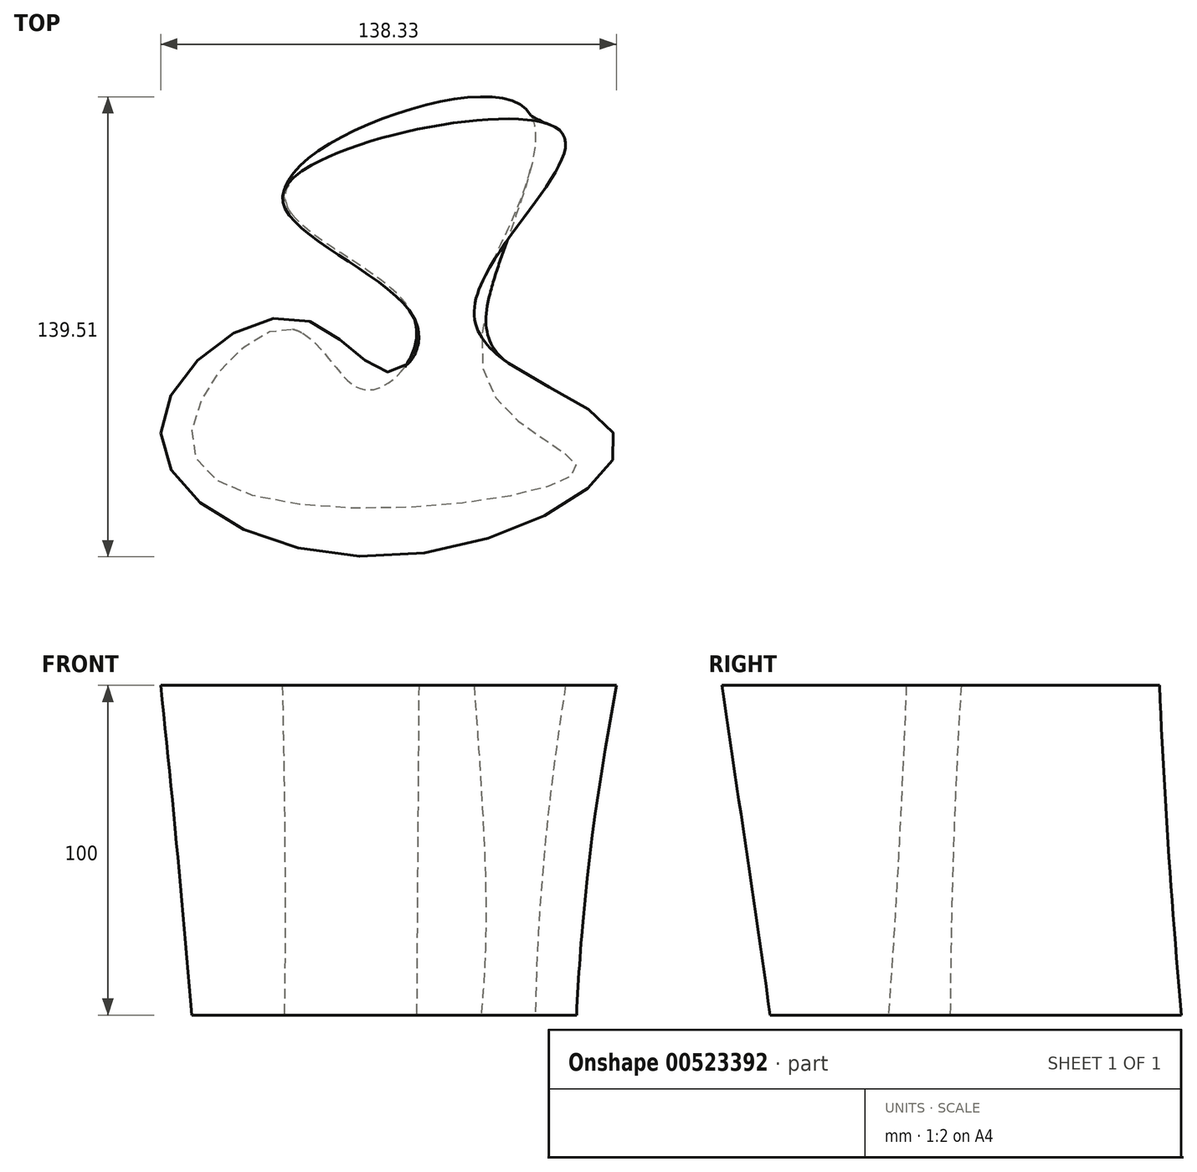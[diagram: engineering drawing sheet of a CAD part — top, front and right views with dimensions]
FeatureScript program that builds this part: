
annotation { "Feature Type Name" : "Feature", "Feature Type Description" : "" }
export const myFeature = defineFeature(function(context is Context, id is Id, definition is map)
    precondition{}
    {
        {
            var Q0;
            Q0=qCreatedBy(makeId("Top.planeOp"),FACE);
            cPlane(context, id + "F0", {"entities" : qUnion([Q0]), "cplaneType" : CPlaneType.OFFSET, "offset" : 100 * mm, "width" : 150 * mm, "height" : 150 * mm});
        }
        {
            var Q0;
            Q0=qCreatedBy(makeId("Top.planeOp"),FACE);
            var sketch = newSketch(context, id + "F1", { "sketchPlane" : qUnion([Q0])});
            skFitSpline(sketch, "E0", {"points": [v(0, 0) * mm, v(-39.28, 38.78) * mm, v(33.62, 63.74) * mm, v(21.63, -18.14) * mm, v(48.93, -46.76) * mm, v(-64.9, -44.77) * mm, v(-38.94, -3.16) * mm, v(-14.98, -21.8) * mm, v(0, 0) * mm]});
            skSolve(sketch);
        }
        {
            var Q0;
            Q0=qCreatedBy(id+"F0.planeOp",FACE);
            var sketch = newSketch(context, id + "F2", { "sketchPlane" : qUnion([Q0])});
            skFitSpline(sketch, "E1", {"points": [v(0, 0) * mm, v(-39.6, 38.44) * mm, v(44.93, 56.08) * mm, v(18.3, 0) * mm, v(60.91, -35.78) * mm, v(-8.99, -72.4) * mm, v(-76.89, -34.12) * mm, v(-35.95, 0) * mm, v(-6.99, -16.48) * mm, v(0, 0) * mm]});
            skSolve(sketch);
        }
        {
            var Q0;
            Q0 = qSketchRegion(id + "F1", true);
            var Q1;
            Q1 = qSketchRegion(id + "F2", true);
            loft(context, id + "F3", {"sheetProfilesArray" : [{ "sheetProfileEntities" : qUnion([Q0]) }, { "sheetProfileEntities" : qUnion([Q1]) }]});
        }
    });
